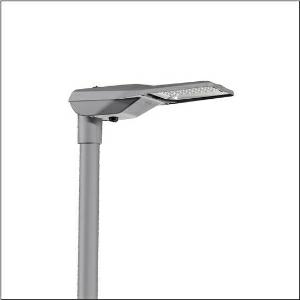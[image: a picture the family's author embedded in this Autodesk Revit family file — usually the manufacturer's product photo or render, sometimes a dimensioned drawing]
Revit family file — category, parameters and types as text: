
# Revit family: streetlight_sl_21_mini___p0_8ab_5xe2r33t08hb_4a65
name_source: partatom
category: Lighting Fixtures
units: mm (PartAtom-declared; Revit-internal decimal feet)

## family parameters
Cut with Voids When Loaded = No
Host = Face
Light Source = No
Part Type = Normal
Room Calculation Point = No
Round Connector Dimension = Use Diameter
Shared = No

## types (1)
- --- (1 x LED, 7850 lm, 66 W, 3000K)
    Apparent Load = 66 VA
    CIE Flux Codes = 36 71 98 100 100
    Color Rendering = 70
    Color Temperature = 3000K
    Default Elevation = 1800 mm
    Description = Streetlight SL 21 mini, mast luminaire, primary light control with lens, of PMMA, primary optical cover: cover, of toughened safety glass, transparent, light distribution: P0.8aB, light emission: direct distribution, primary light characteristic: asymmetric, installation type: post-top, side-entry, LED, High Power LED, rated luminous flux: 7.850lm, luminous efficacy: 119lm/W, light colour: 730, colour temperature: 3000K, control gear: D4i, control: pre-setting: logarithmic dimming characteristic, flexible luminous flux parameterisation, time-dependent luminous flux control, constant luminous flux control, overheat protection, mains connection: 220..240V, AC, 50/60Hz, start of lifetime: 66W, end of service life: 69W, reduction: 30W, luminaire housing, of diecast aluminium, powder-coated, Siteco® metallic grey (DB 702S), corrosivity category C5 mid according to DIN EN ISO 12944, multi-level sealing system, sealing non-destructively replaceable, inclination adjustable: 0°, 5°, 10°, 15°, please order mast flange separately, length: 628mm, width: 235mm, height: 110mm, mast flange for spigot size: 42mm (side-entry): 5XC10008XM4, 60/48mm (side-entry/post-top): 5XC10108XM2, 76/60mm (side-entry/post-top): 5XC10108XM1, mounting height: 4..8m, Smart Interface below and above, protection rating (complete): IP66, insulation class (complete): insulation class II (safety insulation), certification: CE, ENEC, ENEC+, VDE, impact resistance: IK10, permissible operating ambient temperature for outdoor applications: -40..+50°C, standard-compliant lighting for roads and squares, packaging unit: 1 piece

Light Distribution: P0.8aB
    Height = 110 mm
    Lamp = 1 x LED
    Lamp Light Flux = 7850 lm
    Lamp Power = 66 W
    Lamp count = 1
    Length = 625 mm
    Luminous efficacy = 119 lm/W
    Manufacturer = Siteco
    ModVariant = No
    Model = 5XE2R33T08HB
    Number of Poles = 1
    OnlyDefault = Yes
    Power Factor = 1
    Product Name = Streetlight SL 21 mini | P0.8aB
    Product group = mast luminaire | pylon top
    ProductGroupID = 6100
    Protection Class = Protection class II
    Protection Degree = IP 66
    RLX_Detail_Level = 1
    RLX_Emergency_Light_Flux = 0 lm
    RLX_Emergency_Type = 0
    RLX_Emergency_Type_DB = No
    RlxData = <blob elided: 25953 chars, md5=71b95e87>
    Socket = socket
    Standby Power = 0 W
    System Light Flux = 7850 lm
    System Power = 66 W
    Type Comments = factory setting: luminous flux: 100 % | dim-lin: 254 | 670 mA
    Type Image = l_1003514.jpg
    URL = http://relux.com
    VarID = @adj_074860
    Voltage = 0 V
    Weight = 0.00 kg
    Width = 234 mm

## geometry (parser evidence)
native form markers: Blend x4, Sweep x10
no freeform markers — native parametric forms only
